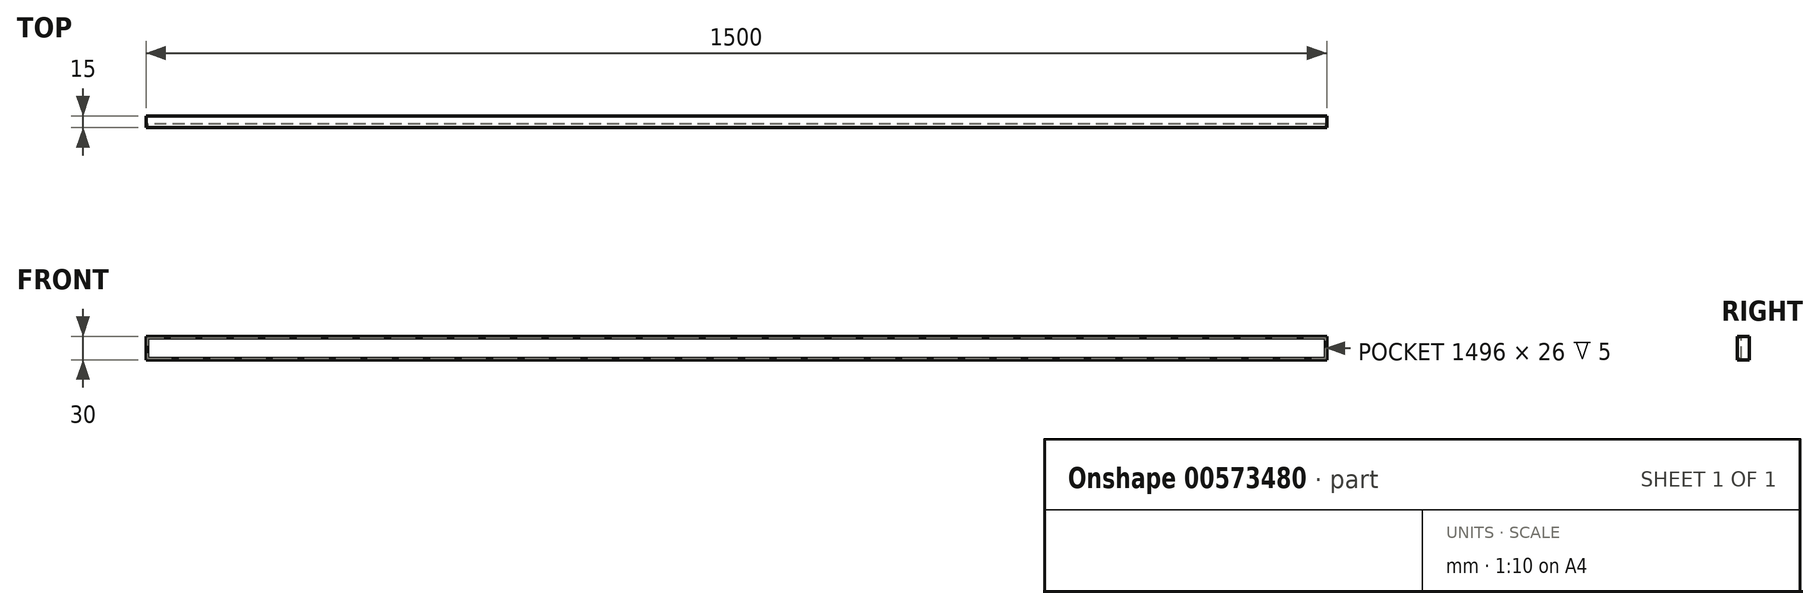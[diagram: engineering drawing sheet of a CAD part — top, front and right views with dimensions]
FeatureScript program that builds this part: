
annotation { "Feature Type Name" : "Feature", "Feature Type Description" : "" }
export const myFeature = defineFeature(function(context is Context, id is Id, definition is map)
    precondition{}
    {
        {
            var Q0;
            Q0=qCreatedBy(makeId("Front.planeOp"),FACE);
            var sketch = newSketch(context, id + "F0", { "sketchPlane" : qUnion([Q0])});
            skLineSegment(sketch, "E0.bottom", {"start": v(750, -15) * mm, "end": v(-750, -15) * mm});
            skLineSegment(sketch, "E0.top", {"start": v(750, 15) * mm, "end": v(-750, 15) * mm});
            skLineSegment(sketch, "E0.left", {"start": v(750, -15) * mm, "end": v(750, 15) * mm});
            skLineSegment(sketch, "E0.right", {"start": v(-750, -15) * mm, "end": v(-750, 15) * mm});
            skPoint(sketch, "E0.middle", {"position": v(0, 0) * mm});
            skSolve(sketch);
        }
        {
            var Q0;
            Q0=makeQuery(id+"F0.imprint","IMPRINT",FACE,{"disambiguationData":[TD([[makeQuery(id+"F0.imprint","IMPRINT",EDGE,{"derivedFrom":sQuery(id+"F0.wireOp",EDGE,"E0.bottom")}),-1.0]])]});
            extrude(context, id + "F1", {"entities" : qUnion([Q0]), "depth" : 15 * mm, "offsetDistance" : 25 * mm});
        }
        {
            var Q0;
            Q0=makeQuery(id+"F1.opExtrude","CAP_FACE",FACE,{"disambiguationData":[OSD([sQuery(id+"F0.wireOp",EDGE,"E0.bottom"),sQuery(id+"F0.wireOp",EDGE,"E0.top"),sQuery(id+"F0.wireOp",EDGE,"E0.left"),sQuery(id+"F0.wireOp",EDGE,"E0.right")])],"isStart":false});
            var sketch = newSketch(context, id + "F2", { "sketchPlane" : qUnion([Q0])});
            skLineSegment(sketch, "E1.bottom", {"start": v(748, -13) * mm, "end": v(-748, -13) * mm});
            skLineSegment(sketch, "E1.top", {"start": v(748, 13) * mm, "end": v(-748, 13) * mm});
            skLineSegment(sketch, "E1.left", {"start": v(748, -13) * mm, "end": v(748, 13) * mm});
            skLineSegment(sketch, "E1.right", {"start": v(-748, -13) * mm, "end": v(-748, 13) * mm});
            skPoint(sketch, "E1.middle", {"position": v(0, 0) * mm});
            skSolve(sketch);
        }
        {
            var Q0;
            Q0 = qSketchRegion(id + "F2", true);
            extrude(context, id + "F3", {"entities" : qUnion([Q0]), "operationType" : NewBodyOperationType.REMOVE, "oppositeDirection" : true, "depth" : 5 * mm, "offsetDistance" : 25 * mm});
        }
    });
